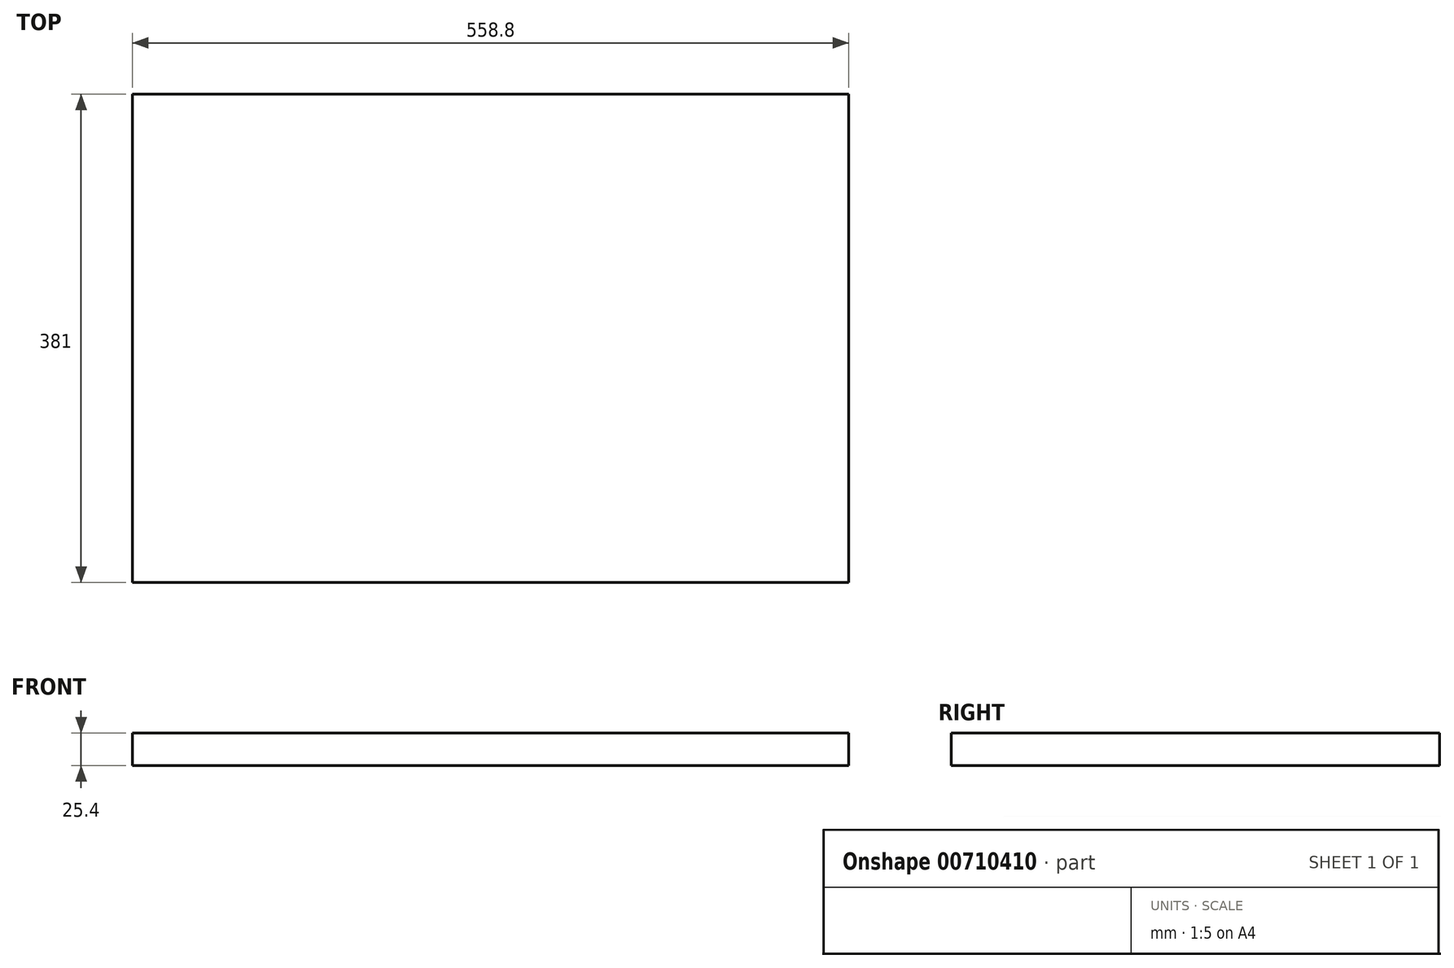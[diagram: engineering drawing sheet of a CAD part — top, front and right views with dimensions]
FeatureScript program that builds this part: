
annotation { "Feature Type Name" : "Feature", "Feature Type Description" : "" }
export const myFeature = defineFeature(function(context is Context, id is Id, definition is map)
    precondition{}
    {
        {
            var Q0;
            Q0=qCreatedBy(makeId("Top.planeOp"),FACE);
            var sketch = newSketch(context, id + "F0", { "sketchPlane" : qUnion([Q0])});
            skPoint(sketch, "E0.middle", {"position": v(0, 0) * mm});
            skLineSegment(sketch, "E1.bottom", {"start": v(-279.4, 190.5) * mm, "end": v(279.4, 190.5) * mm, "construction": true});
            skLineSegment(sketch, "E1.top", {"start": v(-279.4, -190.5) * mm, "end": v(279.4, -190.5) * mm, "construction": true});
            skLineSegment(sketch, "E1.left", {"start": v(-279.4, 190.5) * mm, "end": v(-279.4, -190.5) * mm, "construction": true});
            skLineSegment(sketch, "E1.right", {"start": v(279.4, 190.5) * mm, "end": v(279.4, -190.5) * mm, "construction": true});
            skLineSegment(sketch, "E2.bottom", {"start": v(-279.4, 190.5) * mm, "end": v(279.4, 190.5) * mm});
            skLineSegment(sketch, "E2.top", {"start": v(-279.4, -190.5) * mm, "end": v(279.4, -190.5) * mm});
            skLineSegment(sketch, "E2.left", {"start": v(-279.4, 190.5) * mm, "end": v(-279.4, -190.5) * mm});
            skLineSegment(sketch, "E2.right", {"start": v(279.4, 190.5) * mm, "end": v(279.4, -190.5) * mm});
            skSolve(sketch);
        }
        {
            var Q0;
            Q0=makeQuery(id+"F0.imprint","IMPRINT",FACE,{"disambiguationData":[TD([[makeQuery(id+"F0.imprint","IMPRINT",EDGE,{"derivedFrom":sQuery(id+"F0.wireOp",EDGE,"E2.bottom")}),-1.0]])]});
            extrude(context, id + "F1", {"entities" : qUnion([Q0]), "oppositeDirection" : true, "depth" : 25.4 * mm, "offsetDistance" : 25.4 * mm});
        }
    });
